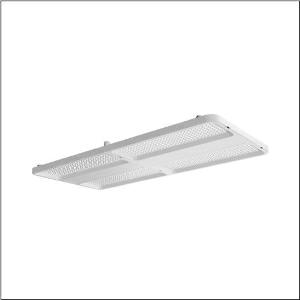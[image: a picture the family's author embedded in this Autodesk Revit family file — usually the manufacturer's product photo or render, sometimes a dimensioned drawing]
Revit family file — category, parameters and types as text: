
# Revit family: highbay_21_maxi_52hn12db6lda
name_source: partatom
category: Lighting Fixtures
units: mm (PartAtom-declared; Revit-internal decimal feet)

## family parameters
Cut with Voids When Loaded = No
Host = Face
Light Source = No
Part Type = Normal
Room Calculation Point = No
Round Connector Dimension = Use Diameter
Shared = No

## types (1)
- --- (1 x LED, 4100 lm, 22.6 W, 6500K)
    Apparent Load = 23 VA
    CIE Flux Codes = 90 98 100 100 100
    Color Rendering = 80
    Color Temperature = 6500K
    Default Elevation = 1800 mm
    Description = high bay luminaire Highbay 21 maxi; direct symmetric wide distribution, light control with lens of PMMA; UGR ≤ 22 (X = 4H | Y = 8H | S = 0.25H | reflection values 70/50/20); luminous flux: 27.140lm; light colour: 865, colour temperature: 6500K, MacAdam ≤ 3 SDCM (initial), colour rendering: CRI > 80; luminous efficacy: 188,5lm/W; rated service life: 75.000h (L80) at AT= ta max; control: DALI 2; luminaire connection: terminal, 5-pole, max. 2.5mm² (cable entry for one cable, Ø 8.5..16mm); mains connection: 230..240V, AC/DC 0/50..60Hz; connected load: 144W; protection rating (complete): IP66; insulation class (complete): insulation class I (protective earthing); protection symbol: D; impact resistance: IK08; certification: CE, ENEC, VDE, UKCA; luminaire for central battery installations according to EN 60598-2-22, internal wiring halogen-free; luminaire LABS conformity tested according to VDMA 24364:2018-05; Suitable for use in the food industry according to the specifications of IFS-Food, HACCP and/or BRC; housing frame of high-performance plastic PA6, matt traffic white (RAL 9016); cover of PMMA; dimension (LxWxH): 946 x 442 x 72mm; permissible operating ambient temperature: -40..+65°C (reducing of maximum allowable ambient temperature of 5°C with ceiling mounting); packaging unit: 1 piece; (delivery without accessories; please order mounting accessories separately)
    Height = 72 mm  [stored 0.23622 ft]
    Lamp = 1 x LED
    Lamp Light Flux = 4100 lm
    Lamp Power = 22.6 W
    Lamp count = 1
    Length = 946 mm
    Luminous efficacy = 181 lm/W
    Manufacturer = Siteco
    ModVariant = No
    Model = 52HN12DB6LDA
    Mounting Place = Ceiling
    Mounting Type = Pendant
    Number of Poles = 1
    OnlyDefault = Yes
    Power Factor = 1
    Product Name = Highbay 21 maxi
    Product group = high bay luminaire
    ProductGroupID = 902
    Protection Class = Protection class I
    Protection Degree = IP 66
    RLX_Detail_Level = 1
    RLX_Emergency_Light_Flux = 0 lm
    RLX_Emergency_Type = 0
    RLX_Emergency_Type_DB = No
    RlxData = <blob elided: 128589 chars, md5=82895921>
    Socket = socket
    Standby Power = 0 W
    System Light Flux = 4100 lm
    System Power = 23 W
    Type Comments = : DC mode (central or group accumulator) initial emergency light level
    Type Image = l_1363244.jpg
    URL = http://relux.com
    VarID = @adj_004881
    Voltage = 0 V
    Weight = 0.00 kg
    Width = 442 mm

note: [stored X ft] marks values corroborated as IEEE doubles in the binary element streams (Revit-internal decimal feet)

## geometry (parser evidence)
native form markers: Blend x4, Sweep x9
no freeform markers — native parametric forms only
